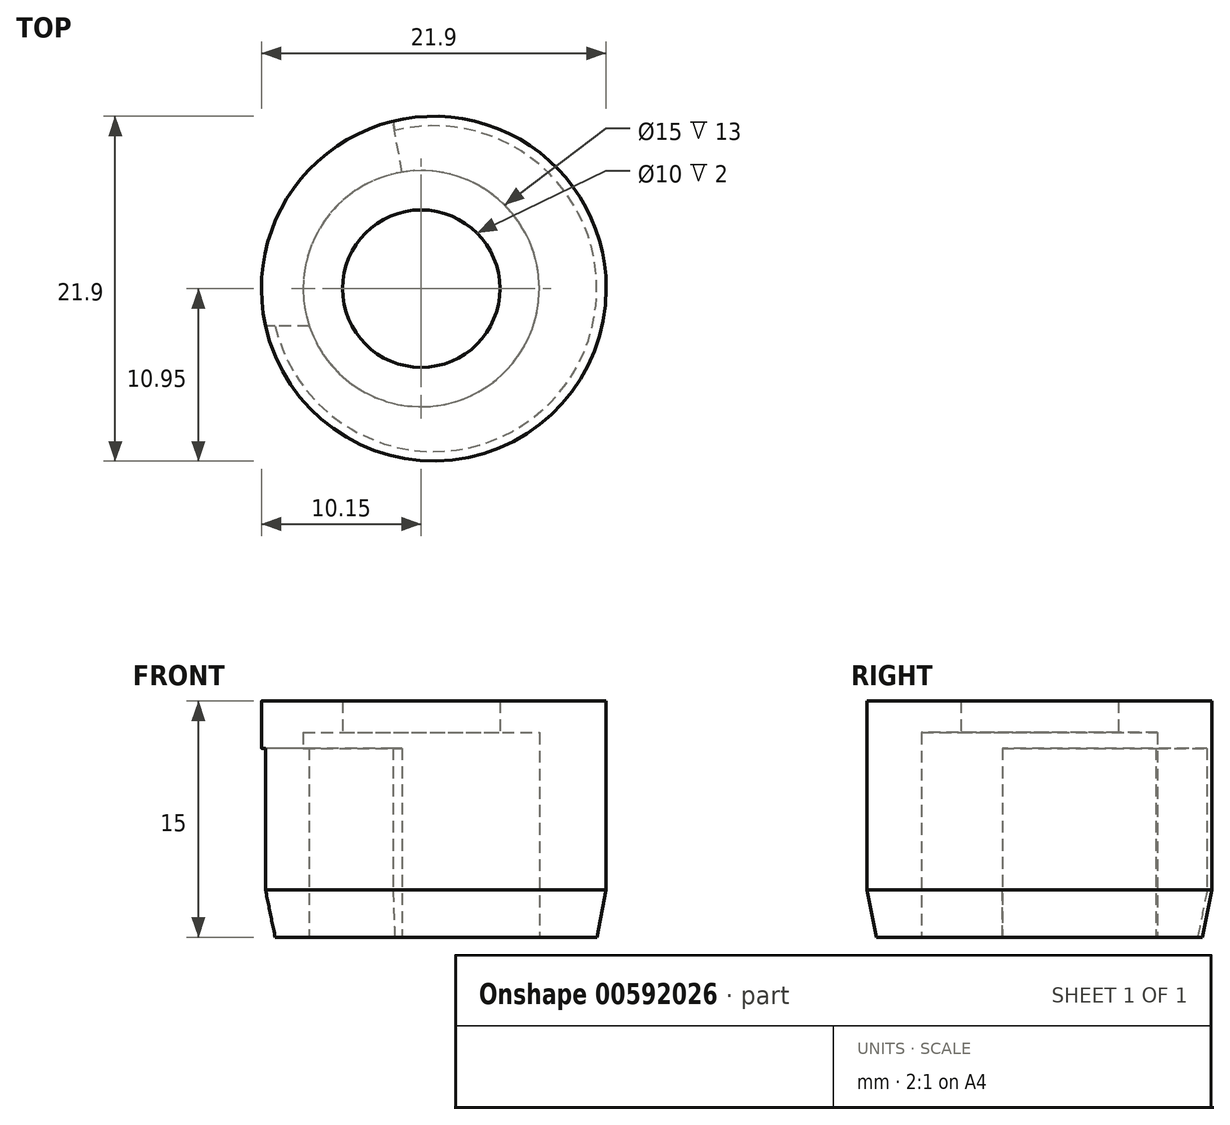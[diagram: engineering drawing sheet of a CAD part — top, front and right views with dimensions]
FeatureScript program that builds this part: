
annotation { "Feature Type Name" : "Feature", "Feature Type Description" : "" }
export const myFeature = defineFeature(function(context is Context, id is Id, definition is map)
    precondition{}
    {
        {
            var Q0;
            Q0=qCreatedBy(makeId("Top.planeOp"),FACE);
            var sketch = newSketch(context, id + "F0", { "sketchPlane" : qUnion([Q0])});
            skCircle(sketch, "E0", {"center": v(0, 0) * mm, "radius": 10.95 * mm});
            skSolve(sketch);
        }
        {
            var Q0;
            Q0=makeQuery(id+"F0.imprint","IMPRINT",FACE,{"disambiguationData":[TD([[makeQuery(id+"F0.imprint","IMPRINT",EDGE,{"derivedFrom":sQuery(id+"F0.wireOp",EDGE,"E0")}),1.0]])]});
            extrude(context, id + "F1", {"entities" : qUnion([Q0]), "depth" : 15 * mm, "offsetDistance" : 25 * mm});
        }
        {
            var Q0;
            Q0=makeQuery(id+"F1.opExtrude","CAP_FACE",FACE,{"disambiguationData":[OSD([sQuery(id+"F0.wireOp",EDGE,"E0")])],"isStart":true});
            var sketch = newSketch(context, id + "F2", { "sketchPlane" : qUnion([Q0])});
            skCircle(sketch, "E1", {"center": v(-0.8, 0) * mm, "radius": 7.5 * mm});
            skLineSegment(sketch, "E2", {"start": v(-7.92, 2.37) * mm, "end": v(-10.7, 2.37) * mm});
            skLineSegment(sketch, "E3", {"start": v(-2.02, -7.4) * mm, "end": v(-2.6, -10.64) * mm});
            skSolve(sketch);
        }
        {
            var Q0;
            {var subQ0=sQuery(id+"F2.wireOp",EDGE,"E2");Q0=makeQuery(id+"F2.imprint","IMPRINT",FACE,{"disambiguationData":[TD([[makeQuery(id+"F2.imprint","IMPRINT",EDGE,{"derivedFrom":subQ0}),1.0]])]});}
            extrude(context, id + "F3", {"entities" : qUnion([Q0]), "operationType" : NewBodyOperationType.REMOVE, "oppositeDirection" : true, "depth" : 12 * mm, "offsetDistance" : 25 * mm});
        }
        {
            var Q0;
            Q0 = qSketchRegion(id + "F2", true);
            extrude(context, id + "F4", {"entities" : qUnion([Q0]), "operationType" : NewBodyOperationType.REMOVE, "oppositeDirection" : true, "depth" : 13 * mm, "offsetDistance" : 25 * mm});
        }
        {
            var Q0;
            Q0=makeQuery(id+"F4.boolean.opBoolean","COPY",FACE,{"derivedFrom":makeQuery(id+"F4.opExtrude","CAP_FACE",FACE,{"disambiguationData":[OSD([sQuery(id+"F2.wireOp",EDGE,"E1")])],"isStart":false})});
            var sketch = newSketch(context, id + "F5", { "sketchPlane" : qUnion([Q0])});
            skPoint(sketch, "E4", {"position": v(-0.8, 0) * mm});
            skSolve(sketch);
        }
        {
            var Q0;
            Q0=sQuery(id+"F5.wireOp",VERTEX,"E4");
            var Q1;
            Q1=makeQuery(id+"F1.opExtrude","SWEPT_BODY",BODY,{"disambiguationData":[OSD([sQuery(id+"F0.wireOp",EDGE,"E0")])]});
            hole(context, id + "F6", {"style" : HoleStyle.SIMPLE, "endStyle" : HoleEndStyle.BLIND, "holeDiameter" : 10 * mm, "majorDiameter" : 5 * mm, "holeDepth" : 10 * mm, "isTappedThrough" : true, "tappedDepth" : 12 * mm, "tapClearance" : 3, "locations" : qUnion([Q0]), "scope" : qUnion([Q1])});
        }
        {
            var Q0;
            Q0=makeQuery(id+"F1.opExtrude","CAP_EDGE",EDGE,{"disambiguationData":[OSD([sQuery(id+"F0.wireOp",EDGE,"E0")])],"isStart":true});
            chamfer(context, id + "F7", {"entities" : qUnion([Q0]), "chamferType" : ChamferType.TWO_OFFSETS, "width1" : 3 * mm, "oppositeDirection" : false, "width2" : 0.6 * mm, "tangentPropagation" : true});
        }
    });
